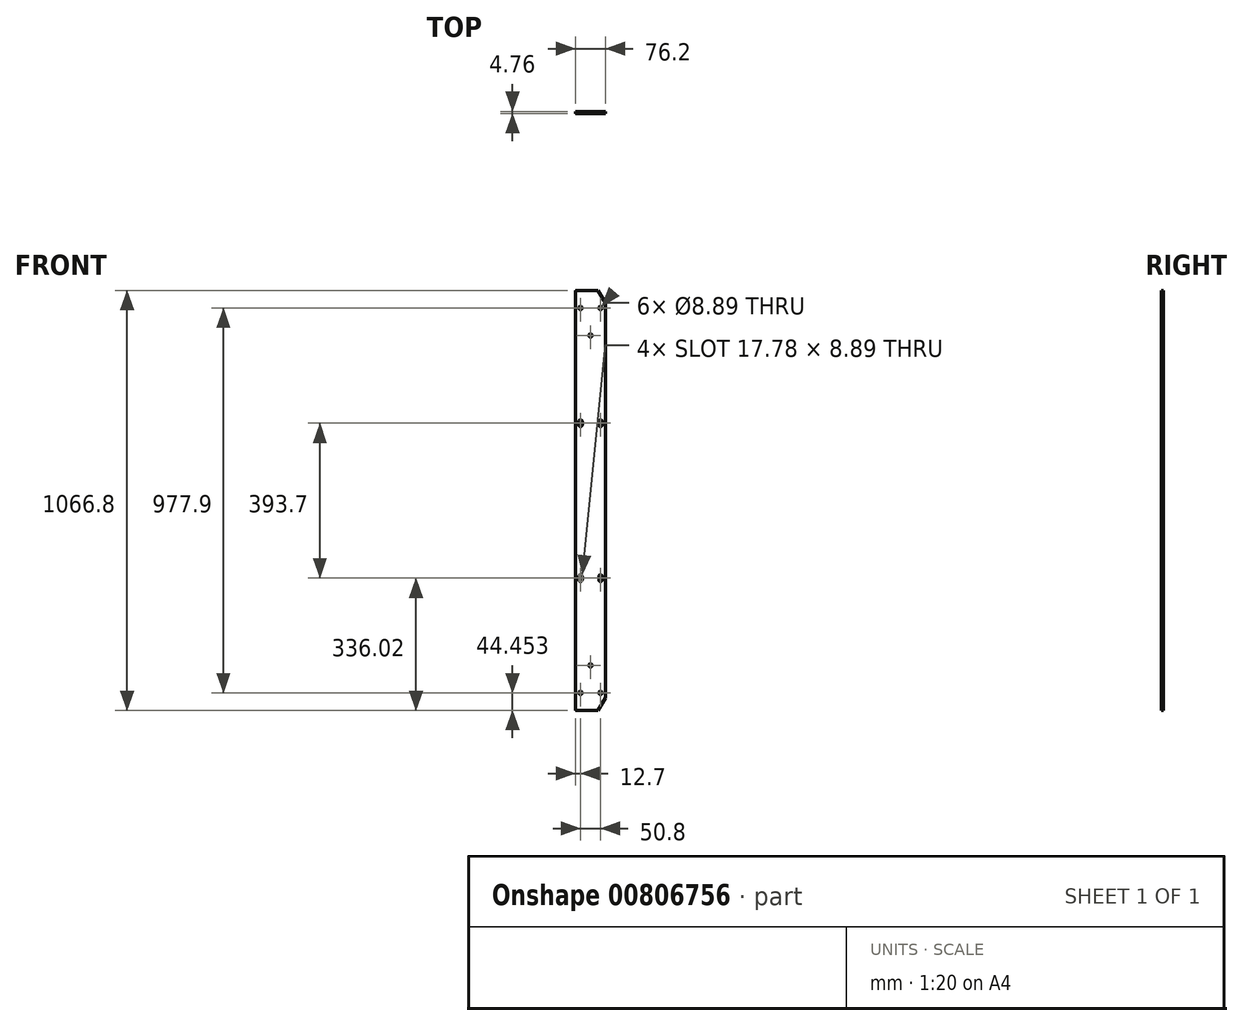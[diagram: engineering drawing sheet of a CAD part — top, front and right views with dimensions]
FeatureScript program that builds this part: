
annotation { "Feature Type Name" : "Feature", "Feature Type Description" : "" }
export const myFeature = defineFeature(function(context is Context, id is Id, definition is map)
    precondition{}
    {
        {
            var Q0;
            Q0=qCreatedBy(makeId("Front.planeOp"),FACE);
            var sketch = newSketch(context, id + "F0", { "sketchPlane" : qUnion([Q0])});
            skLineSegment(sketch, "E0.bottom", {"start": v(-1066.8, -1034.52) * mm, "end": v(-1066.8, -31.22) * mm});
            skLineSegment(sketch, "E0.top", {"start": v(-1143, -1064.74) * mm, "end": v(-1143, -1) * mm});
            skLineSegment(sketch, "E0.left", {"start": v(-1085.85, -1066.27) * mm, "end": v(-1141.48, -1066.27) * mm});
            skLineSegment(sketch, "E0.right", {"start": v(-1085.85, 0.53) * mm, "end": v(-1141.48, 0.53) * mm});
            skCircle(sketch, "E1", {"center": v(-1130.3, -1021.82) * mm, "radius": 4.45 * mm});
            skCircle(sketch, "E2", {"center": v(-1079.5, -1021.82) * mm, "radius": 4.45 * mm});
            skCircle(sketch, "E3", {"center": v(-1104.9, -951.97) * mm, "radius": 4.45 * mm});
            skCircle(sketch, "E4", {"center": v(-1104.9, -113.77) * mm, "radius": 4.45 * mm});
            skCircle(sketch, "E5", {"center": v(-1130.3, -43.92) * mm, "radius": 4.45 * mm});
            skCircle(sketch, "E6", {"center": v(-1079.5, -43.92) * mm, "radius": 4.45 * mm});
            skPoint(sketch, "E7.orphan", {"position": v(-1143, 0.53) * mm});
            skPoint(sketch, "E8.orphan", {"position": v(-1143, -1066.27) * mm});
            skPoint(sketch, "E9.visualSharp", {"position": v(-1066.8, -1066.27) * mm});
            skPoint(sketch, "E10.visualSharp", {"position": v(-1143, -1021.82) * mm});
            skPoint(sketch, "E11.visualSharp", {"position": v(-1143, -43.92) * mm});
            skPoint(sketch, "E12.visualSharp", {"position": v(-1066.8, 0.53) * mm});
            skArc(sketch, "E13", {"start": v(-1125.86, -332.1) * mm, "mid": v(-1130.3, -327.66) * mm, "end": v(-1134.75, -332.1) * mm});
            skArc(sketch, "E14", {"start": v(-1075.06, -332.1) * mm, "mid": v(-1079.5, -327.66) * mm, "end": v(-1083.95, -332.1) * mm});
            skArc(sketch, "E15", {"start": v(-1083.95, -341) * mm, "mid": v(-1079.5, -345.44) * mm, "end": v(-1075.06, -341) * mm});
            skArc(sketch, "E16", {"start": v(-1134.75, -341) * mm, "mid": v(-1130.3, -345.44) * mm, "end": v(-1125.86, -341) * mm});
            skArc(sketch, "E17", {"start": v(-1125.86, -725.8) * mm, "mid": v(-1130.3, -721.36) * mm, "end": v(-1134.75, -725.8) * mm});
            skArc(sketch, "E18", {"start": v(-1075.06, -725.8) * mm, "mid": v(-1079.5, -721.36) * mm, "end": v(-1083.95, -725.8) * mm});
            skArc(sketch, "E19", {"start": v(-1083.95, -734.7) * mm, "mid": v(-1079.5, -739.14) * mm, "end": v(-1075.06, -734.7) * mm});
            skArc(sketch, "E20", {"start": v(-1134.75, -734.7) * mm, "mid": v(-1130.3, -739.14) * mm, "end": v(-1125.86, -734.7) * mm});
            skLineSegment(sketch, "E21", {"start": v(-1134.75, -725.8) * mm, "end": v(-1134.75, -734.7) * mm});
            skLineSegment(sketch, "E22", {"start": v(-1125.86, -725.8) * mm, "end": v(-1125.86, -734.7) * mm});
            skLineSegment(sketch, "E23", {"start": v(-1083.95, -725.8) * mm, "end": v(-1083.95, -734.7) * mm});
            skLineSegment(sketch, "E24", {"start": v(-1075.06, -725.8) * mm, "end": v(-1075.06, -734.7) * mm});
            skLineSegment(sketch, "E25", {"start": v(-1134.75, -332.1) * mm, "end": v(-1134.75, -341) * mm});
            skLineSegment(sketch, "E26", {"start": v(-1125.86, -332.1) * mm, "end": v(-1125.86, -341) * mm});
            skLineSegment(sketch, "E27", {"start": v(-1083.95, -332.1) * mm, "end": v(-1083.95, -341) * mm});
            skLineSegment(sketch, "E28", {"start": v(-1075.06, -332.1) * mm, "end": v(-1075.06, -341) * mm});
            skArc(sketch, "E29.0.filletArc", {"start": v(-1141.48, 0.53) * mm, "mid": v(-1142.55, 0.09) * mm, "end": v(-1143, -1) * mm});
            skArc(sketch, "E29.1.filletArc", {"start": v(-1143, -1064.74) * mm, "mid": v(-1142.55, -1065.82) * mm, "end": v(-1141.48, -1066.27) * mm});
            skLineSegment(sketch, "E30", {"start": v(-1085.85, 0.53) * mm, "end": v(-1066.8, -31.22) * mm});
            skLineSegment(sketch, "E31", {"start": v(-1085.85, -1066.27) * mm, "end": v(-1066.8, -1034.52) * mm});
            skSolve(sketch);
        }
        {
            var Q0;
            Q0=makeQuery(id+"F0.imprint","IMPRINT",FACE,{"disambiguationData":[TD([[makeQuery(id+"F0.imprint","IMPRINT",EDGE,{"derivedFrom":sQuery(id+"F0.wireOp",EDGE,"E0.bottom")}),1.0]])]});
            extrude(context, id + "F1", {"entities" : qUnion([Q0]), "flatOperationType" : FlatOperationType.REMOVE, "depth" : 4.76 * mm, "offsetDistance" : 25.4 * mm, "domain" : OperationDomain.MODEL});
        }
    });
